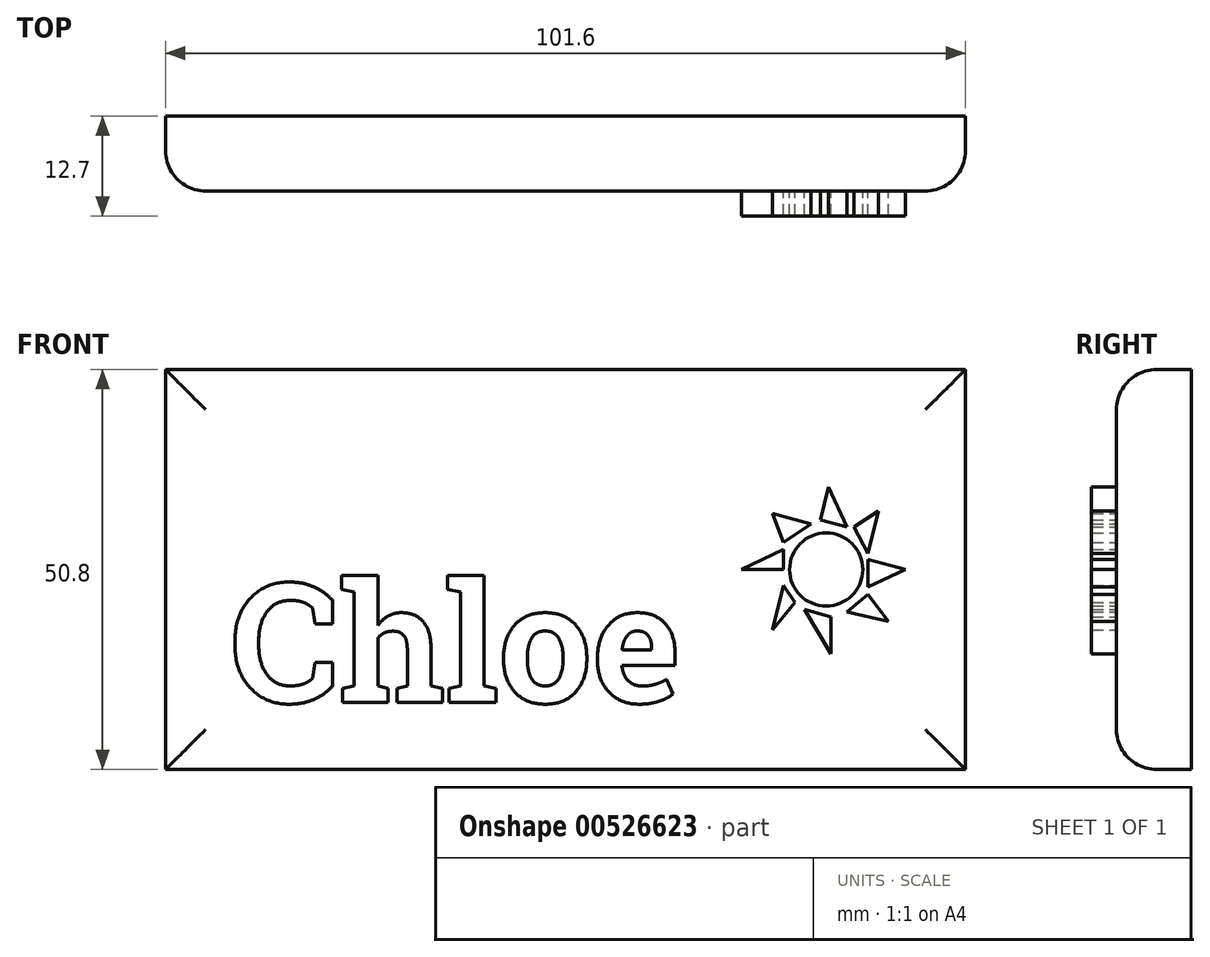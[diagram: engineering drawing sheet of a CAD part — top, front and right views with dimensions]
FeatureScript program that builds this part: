
annotation { "Feature Type Name" : "Feature", "Feature Type Description" : "" }
export const myFeature = defineFeature(function(context is Context, id is Id, definition is map)
    precondition{}
    {
        {
            var Q0;
            Q0=qCreatedBy(makeId("Front.planeOp"),FACE);
            var sketch = newSketch(context, id + "F0", { "sketchPlane" : qUnion([Q0])});
            skLineSegment(sketch, "E0.bottom", {"start": v(-50.8, 25.4) * mm, "end": v(50.8, 25.4) * mm});
            skLineSegment(sketch, "E0.top", {"start": v(-50.8, -25.4) * mm, "end": v(50.8, -25.4) * mm});
            skLineSegment(sketch, "E0.left", {"start": v(-50.8, 25.4) * mm, "end": v(-50.8, -25.4) * mm});
            skLineSegment(sketch, "E0.right", {"start": v(50.8, 25.4) * mm, "end": v(50.8, -25.4) * mm});
            skPoint(sketch, "E0.middle", {"position": v(0, 0) * mm});
            skSolve(sketch);
        }
        {
            var Q0;
            Q0=makeQuery(id+"F0.imprint","IMPRINT",FACE,{"disambiguationData":[TD([[makeQuery(id+"F0.imprint","IMPRINT",EDGE,{"derivedFrom":sQuery(id+"F0.wireOp",EDGE,"E0.bottom")}),-1.0]])]});
            extrude(context, id + "F1", {"entities" : qUnion([Q0]), "depth" : 9.52 * mm, "offsetDistance" : 25.4 * mm});
        }
        {
            var Q0;
            Q0=makeQuery(id+"F1.opExtrude","CAP_EDGE",EDGE,{"disambiguationData":[OSD([sQuery(id+"F0.wireOp",EDGE,"E0.bottom")])],"isStart":false});
            var Q1;
            Q1=makeQuery(id+"F1.opExtrude","CAP_EDGE",EDGE,{"disambiguationData":[OSD([sQuery(id+"F0.wireOp",EDGE,"E0.top")])],"isStart":false});
            var Q2;
            Q2=makeQuery(id+"F1.opExtrude","CAP_EDGE",EDGE,{"disambiguationData":[OSD([sQuery(id+"F0.wireOp",EDGE,"E0.left")])],"isStart":false});
            var Q3;
            Q3=makeQuery(id+"F1.opExtrude","CAP_FACE",FACE,{"disambiguationData":[OSD([sQuery(id+"F0.wireOp",EDGE,"E0.bottom"),sQuery(id+"F0.wireOp",EDGE,"E0.top"),sQuery(id+"F0.wireOp",EDGE,"E0.left"),sQuery(id+"F0.wireOp",EDGE,"E0.right")])],"isStart":false});
            fillet(context, id + "F2", {"entities" : qUnion([Q0, Q1, Q2, Q3]), "radius" : 5.08 * mm, "tangentPropagation" : true, "allowEdgeOverflow" : false});
        }
        {
            var Q0;
            Q0=makeQuery(id+"F1.opExtrude","CAP_FACE",FACE,{"disambiguationData":[OSD([sQuery(id+"F0.wireOp",EDGE,"E0.bottom"),sQuery(id+"F0.wireOp",EDGE,"E0.top"),sQuery(id+"F0.wireOp",EDGE,"E0.left"),sQuery(id+"F0.wireOp",EDGE,"E0.right")])],"isStart":false});
            var sketch = newSketch(context, id + "F3", { "sketchPlane" : qUnion([Q0])});
            skSolve(sketch);
        }
        {
            var Q0;
            {var subQ0=sQuery(id+"F0.wireOp",EDGE,"E0.right");var subQ1=sQuery(id+"F0.wireOp",EDGE,"E0.left");var subQ2=sQuery(id+"F0.wireOp",EDGE,"E0.top");var subQ3=sQuery(id+"F0.wireOp",EDGE,"E0.bottom");var subQ4=makeQuery(id+"F1.opExtrude","CAP_FACE",FACE,{"disambiguationData":[OSD([subQ3,subQ2,subQ1,subQ0])],"isStart":false});Q0=makeQuery(id+"F3.imprint","IMPRINT",FACE,{"disambiguationData":[TD([[makeQuery(id+"F3.imprint","IMPRINT",EDGE,{"derivedFrom":makeQuery(id+"F2.opFillet","BLEND_EDGE",EDGE,{"blendedFrom":[makeQuery(id+"F1.opExtrude","CAP_EDGE",EDGE,{"disambiguationData":[OSD([subQ3])],"isStart":false}),subQ4],"blendedInto":[subQ4]})}),1.0]])]});}
            var sketch = newSketch(context, id + "F4", { "sketchPlane" : qUnion([Q0])});
            skText(sketch, "E1", { "text": "Chloe", "fontName": "RobotoSlab-Bold.ttf"});
            const initialGuessF4  = {"E1": [-0.04254, -0.0169, 1, 0, 0.01528]};
            skSetInitialGuess(sketch, initialGuessF4);
            skSolve(sketch);
        }
        {
            var Q0;
            Q0 = qSketchRegion(id + "F4", true);
            extrude(context, id + "F5", {"entities" : qUnion([Q0]), "operationType" : NewBodyOperationType.REMOVE, "oppositeDirection" : true, "depth" : 1 / 101.6 * mm, "offsetDistance" : 25.4 * mm});
        }
        {
            var Q0;
            {var subQ0=sQuery(id+"F0.wireOp",EDGE,"E0.right");var subQ1=sQuery(id+"F0.wireOp",EDGE,"E0.left");var subQ2=sQuery(id+"F0.wireOp",EDGE,"E0.top");var subQ3=sQuery(id+"F0.wireOp",EDGE,"E0.bottom");var subQ4=makeQuery(id+"F1.opExtrude","CAP_FACE",FACE,{"disambiguationData":[OSD([subQ3,subQ2,subQ1,subQ0])],"isStart":false});Q0=makeQuery(id+"F3.imprint","IMPRINT",FACE,{"disambiguationData":[TD([[makeQuery(id+"F3.imprint","IMPRINT",EDGE,{"derivedFrom":makeQuery(id+"F2.opFillet","BLEND_EDGE",EDGE,{"blendedFrom":[makeQuery(id+"F1.opExtrude","CAP_EDGE",EDGE,{"disambiguationData":[OSD([subQ3])],"isStart":false}),subQ4],"blendedInto":[subQ4]})}),1.0]])]});}
            var sketch = newSketch(context, id + "F6", { "sketchPlane" : qUnion([Q0])});
            skCircle(sketch, "E2", {"center": v(33.1, 0) * mm, "radius": 4.65 * mm});
            skLineSegment(sketch, "E3", {"start": v(32.4, 6.3) * mm, "end": v(35.75, 5.39) * mm});
            skLineSegment(sketch, "E4", {"start": v(35.75, 5.39) * mm, "end": v(33.41, 10.5) * mm});
            skLineSegment(sketch, "E5", {"start": v(33.41, 10.5) * mm, "end": v(32.4, 6.3) * mm});
            skLineSegment(sketch, "E6", {"start": v(38.4, 2.03) * mm, "end": v(39.74, 7.44) * mm});
            skLineSegment(sketch, "E7", {"start": v(39.74, 7.44) * mm, "end": v(36.67, 5.39) * mm});
            skLineSegment(sketch, "E8", {"start": v(36.67, 5.39) * mm, "end": v(38.4, 2.03) * mm});
            skLineSegment(sketch, "E9", {"start": v(38.4, -2.25) * mm, "end": v(43.18, 0) * mm});
            skLineSegment(sketch, "E10", {"start": v(43.18, 0) * mm, "end": v(38.4, 1.3) * mm});
            skLineSegment(sketch, "E11", {"start": v(38.4, 1.3) * mm, "end": v(38.4, -2.25) * mm});
            skLineSegment(sketch, "E12", {"start": v(38.4, -3.17) * mm, "end": v(41.04, -6.63) * mm});
            skLineSegment(sketch, "E13", {"start": v(41.04, -6.63) * mm, "end": v(35.75, -5.39) * mm});
            skLineSegment(sketch, "E14", {"start": v(35.75, -5.39) * mm, "end": v(38.4, -3.17) * mm});
            skLineSegment(sketch, "E15", {"start": v(30.36, -5.1) * mm, "end": v(33.69, -6.01) * mm});
            skLineSegment(sketch, "E16", {"start": v(33.69, -6.01) * mm, "end": v(33.69, -10.7) * mm});
            skLineSegment(sketch, "E17", {"start": v(33.69, -10.7) * mm, "end": v(30.36, -5.1) * mm});
            skLineSegment(sketch, "E18", {"start": v(27.71, -2.05) * mm, "end": v(29.14, -4.19) * mm});
            skLineSegment(sketch, "E19", {"start": v(29.14, -4.19) * mm, "end": v(26.29, -7.65) * mm});
            skLineSegment(sketch, "E20", {"start": v(26.29, -7.65) * mm, "end": v(27.71, -2.05) * mm});
            skLineSegment(sketch, "E21", {"start": v(27.71, 2.53) * mm, "end": v(27.71, 0) * mm});
            skLineSegment(sketch, "E22", {"start": v(27.71, 0) * mm, "end": v(22.32, 0) * mm});
            skLineSegment(sketch, "E23", {"start": v(22.32, 0) * mm, "end": v(27.71, 2.53) * mm});
            skLineSegment(sketch, "E24", {"start": v(27.71, 3.45) * mm, "end": v(31.19, 5.76) * mm});
            skLineSegment(sketch, "E25", {"start": v(31.19, 5.76) * mm, "end": v(26.29, 7.1) * mm});
            skLineSegment(sketch, "E26", {"start": v(26.29, 7.1) * mm, "end": v(27.71, 3.45) * mm});
            skSolve(sketch);
        }
        {
            var Q0;
            Q0=makeQuery(id+"F6.imprint","IMPRINT",FACE,{"disambiguationData":[TD([[makeQuery(id+"F6.imprint","IMPRINT",EDGE,{"derivedFrom":sQuery(id+"F6.wireOp",EDGE,"E9")}),1.0]])]});
            var Q1;
            Q1=makeQuery(id+"F6.imprint","IMPRINT",FACE,{"disambiguationData":[TD([[makeQuery(id+"F6.imprint","IMPRINT",EDGE,{"derivedFrom":sQuery(id+"F6.wireOp",EDGE,"E24")}),1.0]])]});
            var Q2;
            Q2=makeQuery(id+"F6.imprint","IMPRINT",FACE,{"disambiguationData":[TD([[makeQuery(id+"F6.imprint","IMPRINT",EDGE,{"derivedFrom":sQuery(id+"F6.wireOp",EDGE,"E2")}),1.0]])]});
            var Q3;
            Q3=makeQuery(id+"F6.imprint","IMPRINT",FACE,{"disambiguationData":[TD([[makeQuery(id+"F6.imprint","IMPRINT",EDGE,{"derivedFrom":sQuery(id+"F6.wireOp",EDGE,"E3")}),1.0]])]});
            var Q4;
            Q4=makeQuery(id+"F6.imprint","IMPRINT",FACE,{"disambiguationData":[TD([[makeQuery(id+"F6.imprint","IMPRINT",EDGE,{"derivedFrom":sQuery(id+"F6.wireOp",EDGE,"E6")}),1.0]])]});
            var Q5;
            Q5=makeQuery(id+"F6.imprint","IMPRINT",FACE,{"disambiguationData":[TD([[makeQuery(id+"F6.imprint","IMPRINT",EDGE,{"derivedFrom":sQuery(id+"F6.wireOp",EDGE,"E15")}),-1.0]])]});
            var Q6;
            Q6=makeQuery(id+"F6.imprint","IMPRINT",FACE,{"disambiguationData":[TD([[makeQuery(id+"F6.imprint","IMPRINT",EDGE,{"derivedFrom":sQuery(id+"F6.wireOp",EDGE,"E18")}),-1.0]])]});
            var Q7;
            Q7=makeQuery(id+"F6.imprint","IMPRINT",FACE,{"disambiguationData":[TD([[makeQuery(id+"F6.imprint","IMPRINT",EDGE,{"derivedFrom":sQuery(id+"F6.wireOp",EDGE,"E12")}),-1.0]])]});
            var Q8;
            Q8=makeQuery(id+"F6.imprint","IMPRINT",FACE,{"disambiguationData":[TD([[makeQuery(id+"F6.imprint","IMPRINT",EDGE,{"derivedFrom":sQuery(id+"F6.wireOp",EDGE,"E21")}),-1.0]])]});
            extrude(context, id + "F7", {"entities" : qUnion([Q0, Q1, Q2, Q3, Q4, Q5, Q6, Q7, Q8]), "operationType" : NewBodyOperationType.ADD, "depth" : 3.17 * mm, "offsetDistance" : 25.4 * mm});
        }
    });
